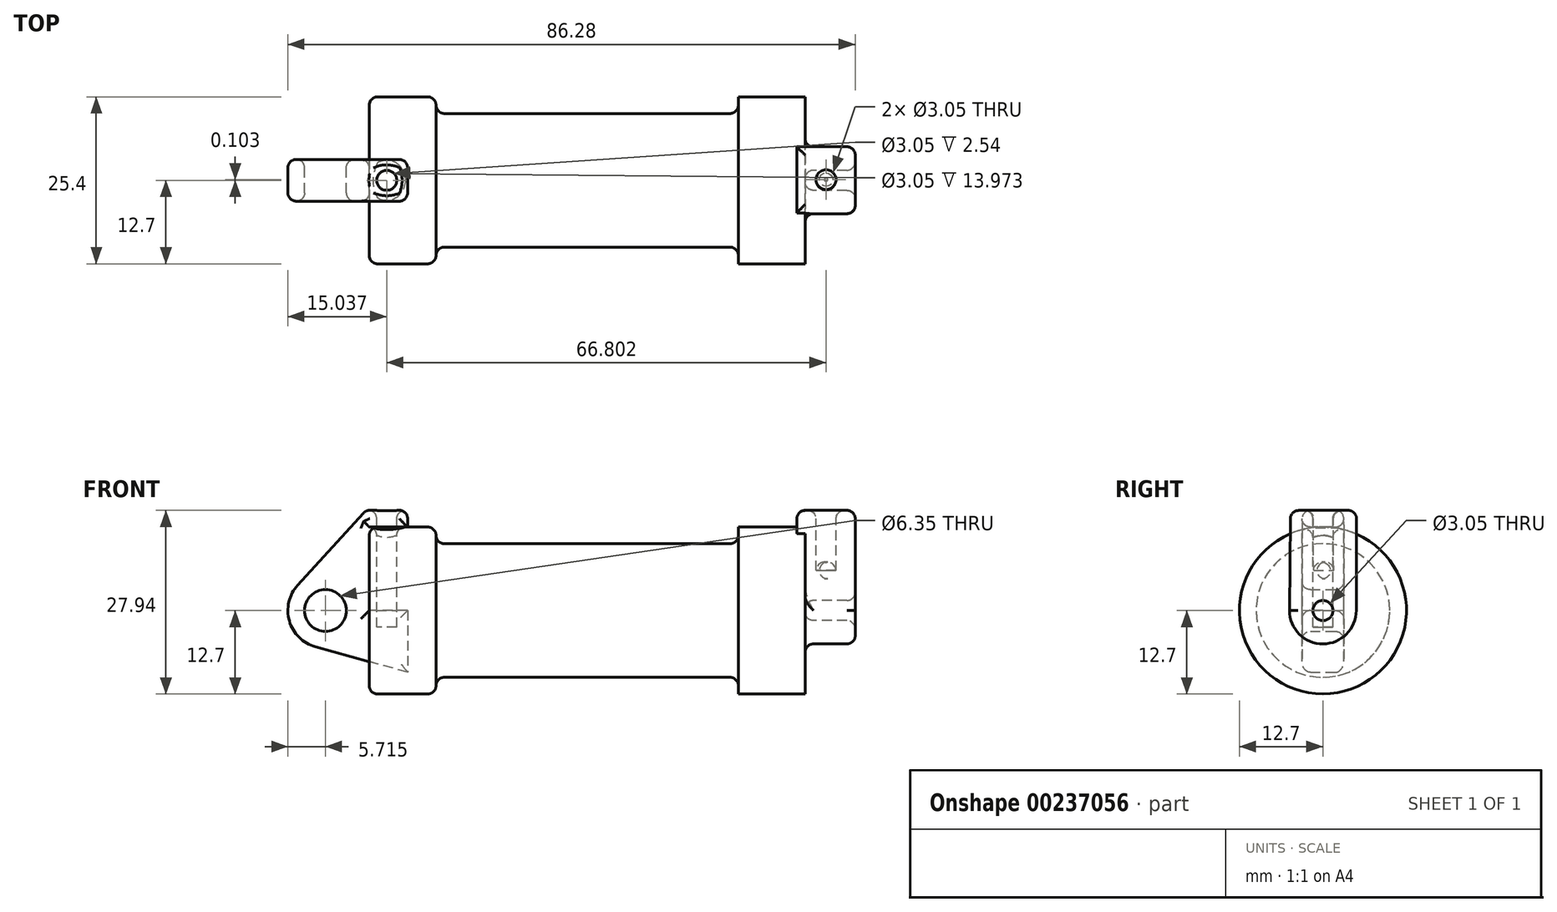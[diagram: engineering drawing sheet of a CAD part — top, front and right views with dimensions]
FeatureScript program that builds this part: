
annotation { "Feature Type Name" : "Feature", "Feature Type Description" : "" }
export const myFeature = defineFeature(function(context is Context, id is Id, definition is map)
    precondition{}
    {
        {
            var Q0;
            Q0=qCreatedBy(makeId("Front.planeOp"),FACE);
            var sketch = newSketch(context, id + "F0", { "sketchPlane" : qUnion([Q0])});
            skLineSegment(sketch, "E0", {"start": v(0, 0) * mm, "end": v(0, 12.7) * mm});
            skLineSegment(sketch, "E1", {"start": v(0, 12.7) * mm, "end": v(10.16, 12.7) * mm});
            skLineSegment(sketch, "E2", {"start": v(10.16, 12.7) * mm, "end": v(10.16, 10.16) * mm});
            skLineSegment(sketch, "E3", {"start": v(10.16, 10.16) * mm, "end": v(56.13, 10.16) * mm});
            skLineSegment(sketch, "E4", {"start": v(56.13, 10.16) * mm, "end": v(56.13, 12.7) * mm});
            skLineSegment(sketch, "E5", {"start": v(56.13, 12.7) * mm, "end": v(66.3, 12.7) * mm});
            skLineSegment(sketch, "E6", {"start": v(66.3, 12.7) * mm, "end": v(66.3, 0) * mm});
            skLineSegment(sketch, "E7", {"start": v(66.3, 0) * mm, "end": v(0, 0) * mm});
            skLineSegment(sketch, "E8", {"start": v(5.84, 15.24) * mm, "end": v(-0.5, 15.24) * mm});
            skLineSegment(sketch, "E9", {"start": v(-0.5, 15.24) * mm, "end": v(-10.88, 3.85) * mm});
            skLineSegment(sketch, "E10", {"start": v(0, 0) * mm, "end": v(-6.65, 0) * mm});
            skCircle(sketch, "E11", {"center": v(-6.65, 0) * mm, "radius": 5.72 * mm});
            skCircle(sketch, "E12", {"center": v(-6.65, 0) * mm, "radius": 3.18 * mm});
            skLineSegment(sketch, "E13", {"start": v(5.84, 15.24) * mm, "end": v(5.84, -9.4) * mm});
            skLineSegment(sketch, "E14", {"start": v(5.84, -9.4) * mm, "end": v(-8.18, -5.5) * mm});
            skSolve(sketch);
        }
        {
            var Q0;
            {var subQ0=sQuery(id+"F0.wireOp",EDGE,"E2");Q0=makeQuery(id+"F0.imprint","IMPRINT",FACE,{"disambiguationData":[TD([[makeQuery(id+"F0.imprint","IMPRINT",EDGE,{"derivedFrom":subQ0}),-1.0]])]});}
            var Q1;
            {var subQ0=sQuery(id+"F0.wireOp",EDGE,"E0");Q1=makeQuery(id+"F0.imprint","IMPRINT",FACE,{"disambiguationData":[TD([[makeQuery(id+"F0.imprint","IMPRINT",EDGE,{"derivedFrom":subQ0}),-1.0]])]});}
            var Q2;
            Q2=sQuery(id+"F0.wireOp",EDGE,"E7");
            revolve(context, id + "F1", {"entities" : qUnion([Q0, Q1]), "axis" : qUnion([Q2]), "revolveType" : RevolveType.FULL});
        }
        {
            var Q0;
            {var subQ3=sQuery(id+"F0.wireOp",EDGE,"E0");Q0=makeQuery(id+"F0.imprint","IMPRINT",FACE,{"disambiguationData":[TD([[makeQuery(id+"F0.imprint","IMPRINT",EDGE,{"derivedFrom":subQ3}),1.0]])]});}
            var Q1;
            {var subQ0=sQuery(id+"F0.wireOp",EDGE,"E14");Q1=makeQuery(id+"F0.imprint","IMPRINT",FACE,{"disambiguationData":[TD([[makeQuery(id+"F0.imprint","IMPRINT",EDGE,{"derivedFrom":subQ0}),-1.0]])]});}
            var Q2;
            {var subQ4=sQuery(id+"F0.wireOp",EDGE,"E12");Q2=makeQuery(id+"F0.imprint","IMPRINT",FACE,{"disambiguationData":[TD([[makeQuery(id+"F0.imprint","IMPRINT",EDGE,{"derivedFrom":subQ4}),-1.0]])]});}
            extrude(context, id + "F2", {"entities" : qUnion([Q0, Q1, Q2]), "endBound" : BoundingType.SYMMETRIC, "depth" : 6.35 * mm});
        }
        {
            var Q0;
            Q0=makeQuery(id+"F1.opRevolve","SWEPT_FACE",FACE,{"disambiguationData":[OSD([sQuery(id+"F0.wireOp",EDGE,"E6")])]});
            var sketch = newSketch(context, id + "F3", { "sketchPlane" : qUnion([Q0])});
            skCircle(sketch, "E15", {"center": v(0, 0) * mm, "radius": 5.08 * mm});
            skCircle(sketch, "E16", {"center": v(0, 0) * mm, "radius": 1.52 * mm});
            skLineSegment(sketch, "E17", {"start": v(5.12, 15.24) * mm, "end": v(5.08, 0) * mm});
            skLineSegment(sketch, "E18", {"start": v(-4.93, 15.22) * mm, "end": v(-5.08, 0) * mm});
            skLineSegment(sketch, "E19", {"start": v(-4.93, 15.22) * mm, "end": v(5.12, 15.24) * mm});
            skSolve(sketch);
        }
        {
            var Q0;
            {var subQ0=sQuery(id+"F3.wireOp",EDGE,"E17");var subQ1=sQuery(id+"F3.wireOp",EDGE,"E15");var subQ2=makeQuery(id+"F3.imprint","INTERSECT",VERTEX,{"derivedFrom":[subQ1,subQ0]});Q0=makeQuery(id+"F3.imprint","IMPRINT",FACE,{"disambiguationData":[TD([[makeQuery(id+"F3.imprint","IMPRINT",EDGE,{"disambiguationData":[TD([[subQ2,-1.0]])],"derivedFrom":subQ1}),-1.0]])]});}
            var Q1;
            {var subQ0=sQuery(id+"F3.wireOp",EDGE,"E19");Q1=makeQuery(id+"F3.imprint","IMPRINT",FACE,{"disambiguationData":[TD([[makeQuery(id+"F3.imprint","IMPRINT",EDGE,{"derivedFrom":subQ0}),-1.0]])]});}
            var Q2;
            Q2=makeQuery(id+"F3.imprint","IMPRINT",FACE,{"disambiguationData":[TD([[makeQuery(id+"F3.imprint","IMPRINT",EDGE,{"derivedFrom":sQuery(id+"F3.wireOp",EDGE,"E16")}),-1.0]])]});
            extrude(context, id + "F4", {"entities" : qUnion([Q0, Q1, Q2]), "operationType" : NewBodyOperationType.ADD, "depth" : 7.62 * mm, "hasSecondDirection" : true, "secondDirectionOppositeDirection" : true, "secondDirectionDepth" : 1.27 * mm});
        }
        {
            var Q0;
            Q0=makeQuery(id+"F2.opExtrude","SWEPT_FACE",FACE,{"disambiguationData":[OSD([sQuery(id+"F0.wireOp",EDGE,"E8")])]});
            var sketch = newSketch(context, id + "F5", { "sketchPlane" : qUnion([Q0])});
            skCircle(sketch, "E20", {"center": v(2.67, 0) * mm, "radius": 1.52 * mm});
            skSolve(sketch);
        }
        {
            var Q0;
            Q0=makeQuery(id+"F5.imprint","IMPRINT",FACE,{"disambiguationData":[TD([[makeQuery(id+"F5.imprint","IMPRINT",EDGE,{"derivedFrom":sQuery(id+"F5.wireOp",EDGE,"E20")}),1.0]])]});
            extrude(context, id + "F6", {"entities" : qUnion([Q0]), "operationType" : NewBodyOperationType.REMOVE, "oppositeDirection" : true, "depth" : 17.78 * mm});
        }
        {
            var Q0;
            Q0=makeQuery(id+"F4.opExtrude","SWEPT_FACE",FACE,{"disambiguationData":[OSD([sQuery(id+"F3.wireOp",EDGE,"E19")])]});
            var sketch = newSketch(context, id + "F7", { "sketchPlane" : qUnion([Q0])});
            skCircle(sketch, "E21", {"center": v(69.47, 0.12) * mm, "radius": 1.52 * mm});
            skSolve(sketch);
        }
        {
            var Q0;
            Q0=makeQuery(id+"F7.imprint","IMPRINT",FACE,{"disambiguationData":[TD([[makeQuery(id+"F7.imprint","IMPRINT",EDGE,{"derivedFrom":sQuery(id+"F7.wireOp",EDGE,"E21")}),1.0]])]});
            extrude(context, id + "F8", {"entities" : qUnion([Q0]), "operationType" : NewBodyOperationType.REMOVE, "oppositeDirection" : true, "depth" : 10.4 * mm});
        }
        {
            var Q0;
            Q0=makeQuery(id+"F2.opExtrude","CAP_EDGE",EDGE,{"disambiguationData":[OSD([sQuery(id+"F0.wireOp",EDGE,"E8")])],"isStart":true});
            var Q1;
            Q1=makeQuery(id+"F2.opExtrude","SWEPT_FACE",FACE,{"disambiguationData":[OSD([sQuery(id+"F0.wireOp",EDGE,"E8")])]});
            var Q2;
            Q2=makeQuery(id+"F2.opExtrude","SWEPT_FACE",FACE,{"disambiguationData":[OSD([sQuery(id+"F0.wireOp",EDGE,"E9")])]});
            var Q3;
            Q3=makeQuery(id+"F2.opExtrude","CAP_FACE",FACE,{"disambiguationData":[OSD([sQuery(id+"F0.wireOp",EDGE,"E0"),sQuery(id+"F0.wireOp",EDGE,"E1"),sQuery(id+"F0.wireOp",EDGE,"E7"),sQuery(id+"F0.wireOp",EDGE,"E8"),sQuery(id+"F0.wireOp",EDGE,"E9"),sQuery(id+"F0.wireOp",EDGE,"E11"),sQuery(id+"F0.wireOp",EDGE,"E12"),sQuery(id+"F0.wireOp",EDGE,"E13"),sQuery(id+"F0.wireOp",EDGE,"E14")])],"isStart":false});
            var Q4;
            Q4=makeQuery(id+"F2.opExtrude","CAP_FACE",FACE,{"disambiguationData":[OSD([sQuery(id+"F0.wireOp",EDGE,"E0"),sQuery(id+"F0.wireOp",EDGE,"E1"),sQuery(id+"F0.wireOp",EDGE,"E7"),sQuery(id+"F0.wireOp",EDGE,"E8"),sQuery(id+"F0.wireOp",EDGE,"E9"),sQuery(id+"F0.wireOp",EDGE,"E11"),sQuery(id+"F0.wireOp",EDGE,"E12"),sQuery(id+"F0.wireOp",EDGE,"E13"),sQuery(id+"F0.wireOp",EDGE,"E14")])],"isStart":true});
            var Q5;
            Q5=makeQuery(id+"F2.opExtrude","SWEPT_FACE",FACE,{"disambiguationData":[OSD([sQuery(id+"F0.wireOp",EDGE,"E12")])]});
            fillet(context, id + "F9", {"entities" : qUnion([Q0, Q1, Q2, Q3, Q4, Q5]), "radius" : 1.27 * mm, "tangentPropagation" : true, "allowEdgeOverflow" : false});
        }
        {
            var Q0;
            Q0=makeQuery(id+"F1.opRevolve","SWEPT_FACE",FACE,{"disambiguationData":[OSD([sQuery(id+"F0.wireOp",EDGE,"E3")])]});
            var Q1;
            Q1=makeQuery(id+"F1.opRevolve","SWEPT_FACE",FACE,{"disambiguationData":[OSD([sQuery(id+"F0.wireOp",EDGE,"E1")])]});
            fillet(context, id + "F10", {"entities" : qUnion([Q0, Q1]), "radius" : 1.27 * mm, "tangentPropagation" : true, "allowEdgeOverflow" : false});
        }
        {
            var Q0;
            Q0=makeQuery(id+"F4.opExtrude","SWEPT_FACE",FACE,{"disambiguationData":[OSD([sQuery(id+"F3.wireOp",EDGE,"E19")])]});
            var Q1;
            Q1=makeQuery(id+"F4.opExtrude","CAP_FACE",FACE,{"disambiguationData":[OSD([sQuery(id+"F3.wireOp",EDGE,"E15"),sQuery(id+"F3.wireOp",EDGE,"E16"),sQuery(id+"F3.wireOp",EDGE,"E17"),sQuery(id+"F3.wireOp",EDGE,"E18"),sQuery(id+"F3.wireOp",EDGE,"E19")])],"isStart":false});
            var Q2;
            Q2=makeQuery(id+"F4.opExtrude","SWEPT_FACE",FACE,{"disambiguationData":[OSD([sQuery(id+"F3.wireOp",EDGE,"E15")])]});
            var Q3;
            Q3=makeQuery(id+"F4.opExtrude","SWEPT_FACE",FACE,{"disambiguationData":[OSD([sQuery(id+"F3.wireOp",EDGE,"E16")])]});
            var Q4;
            Q4=makeQuery(id+"F8.boolean.opBoolean","COPY",FACE,{"derivedFrom":makeQuery(id+"F8.opExtrude","SWEPT_FACE",FACE,{"disambiguationData":[OSD([sQuery(id+"F7.wireOp",EDGE,"E21")])]})});
            fillet(context, id + "F11", {"entities" : qUnion([Q0, Q1, Q2, Q3, Q4]), "radius" : 1.27 * mm, "tangentPropagation" : true, "allowEdgeOverflow" : false});
        }
    });
